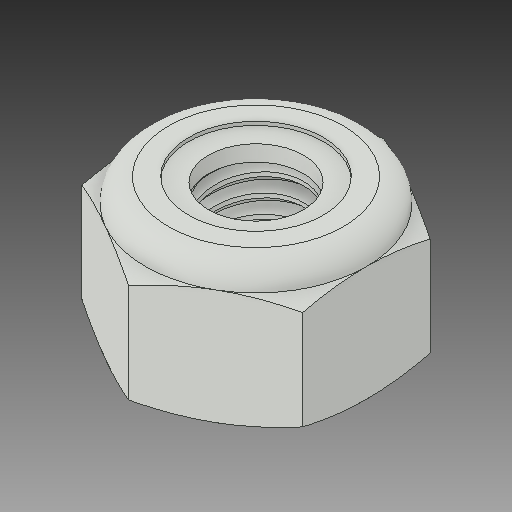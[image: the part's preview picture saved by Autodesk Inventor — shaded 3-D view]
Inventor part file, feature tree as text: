
AUTODESK INVENTOR PART (.ipt)
format: ipt  version: 2019 (Build 230136000, 136)  size: 333,312 bytes
history: native  units: in
note: dims shown in document units (in); Inventor stores cm internally (conversion verified against a paired STEP export)
features: other x1, revolve x1
ambient origin geometry x8: Origin, YZ Plane, XZ Plane, XY Plane, X Axis, Y Axis, Z Axis, Center Point
bodies: Solid1 (feature_tree), Solid2 (feature_tree)
feature tree (2):
  other  "Cut-Revolve4"
  revolve  "Revolve2"  [1 undecoded]
note: 1 required parameter value undecoded (feature->parameter linkage not recoverable at this tier; creation-order binding heuristic only, values carry confidence <= 0.55)
